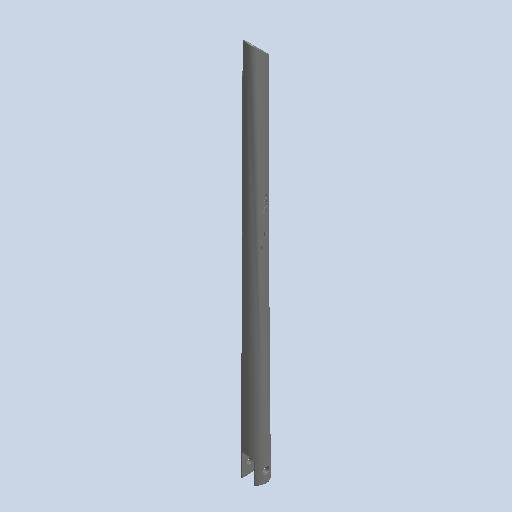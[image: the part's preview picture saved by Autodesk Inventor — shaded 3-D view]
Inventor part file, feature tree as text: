
AUTODESK INVENTOR PART (.ipt)
format: ipt  version: 2022.1 (Build 261234000, 234)  size: 611,840 bytes
history: mixed  units: mm (DEFAULTED — no unit token found)
features: other x8, fillet x1, imported_body x1
bodies: Body1 (imported_parasolid)
feature tree (10):
  other  "Sólido1"
  other  "Origen"
  other  "Plano YZ"
  other  "Plano XZ"
  other  "Plano XY"
  other  "Eje X"
  other  "Eje Y"
  other  "Eje Z"
  fillet  "Fillet4"  [1 undecoded]
  imported_body  NMx_Import_Brep_tag  [imported B-rep: ~2 faces, bbox_mm=None]
note: 1 required parameter value undecoded (feature->parameter linkage not recoverable at this tier; creation-order binding heuristic only, values carry confidence <= 0.55)
